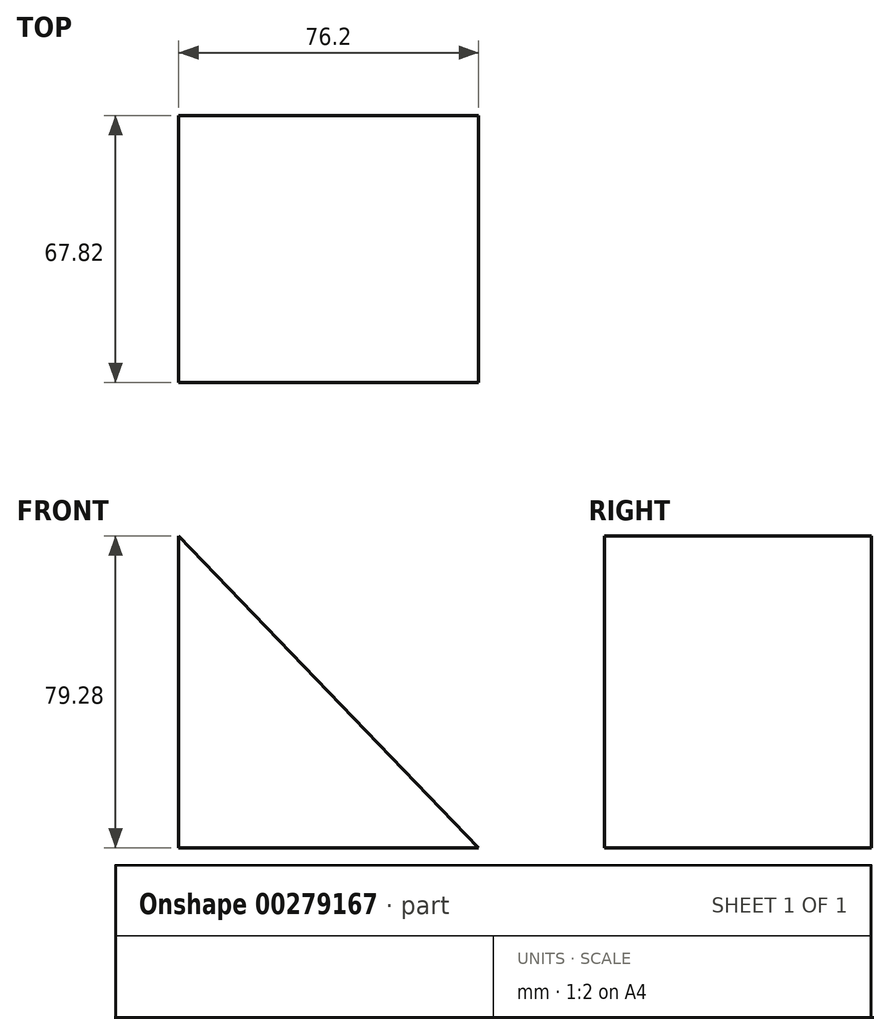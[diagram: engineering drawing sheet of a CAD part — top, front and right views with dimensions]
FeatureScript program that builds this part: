
annotation { "Feature Type Name" : "Feature", "Feature Type Description" : "" }
export const myFeature = defineFeature(function(context is Context, id is Id, definition is map)
    precondition{}
    {
        {
            var Q0;
            Q0=qCreatedBy(makeId("Front.planeOp"),FACE);
            var sketch = newSketch(context, id + "F0", { "sketchPlane" : qUnion([Q0])});
            skLineSegment(sketch, "E0", {"start": v(-76.37, 75.64) * mm, "end": v(-76.37, -3.64) * mm});
            skLineSegment(sketch, "E1", {"start": v(-76.37, -3.64) * mm, "end": v(-0.17, -3.64) * mm});
            skLineSegment(sketch, "E2", {"start": v(-0.17, -3.64) * mm, "end": v(-76.37, 75.64) * mm});
            skSolve(sketch);
        }
        {
            var Q0;
            Q0 = qSketchRegion(id + "F0", true);
            extrude(context, id + "F1", {"entities" : qUnion([Q0]), "depth" : 67.82 * mm});
        }
    });
